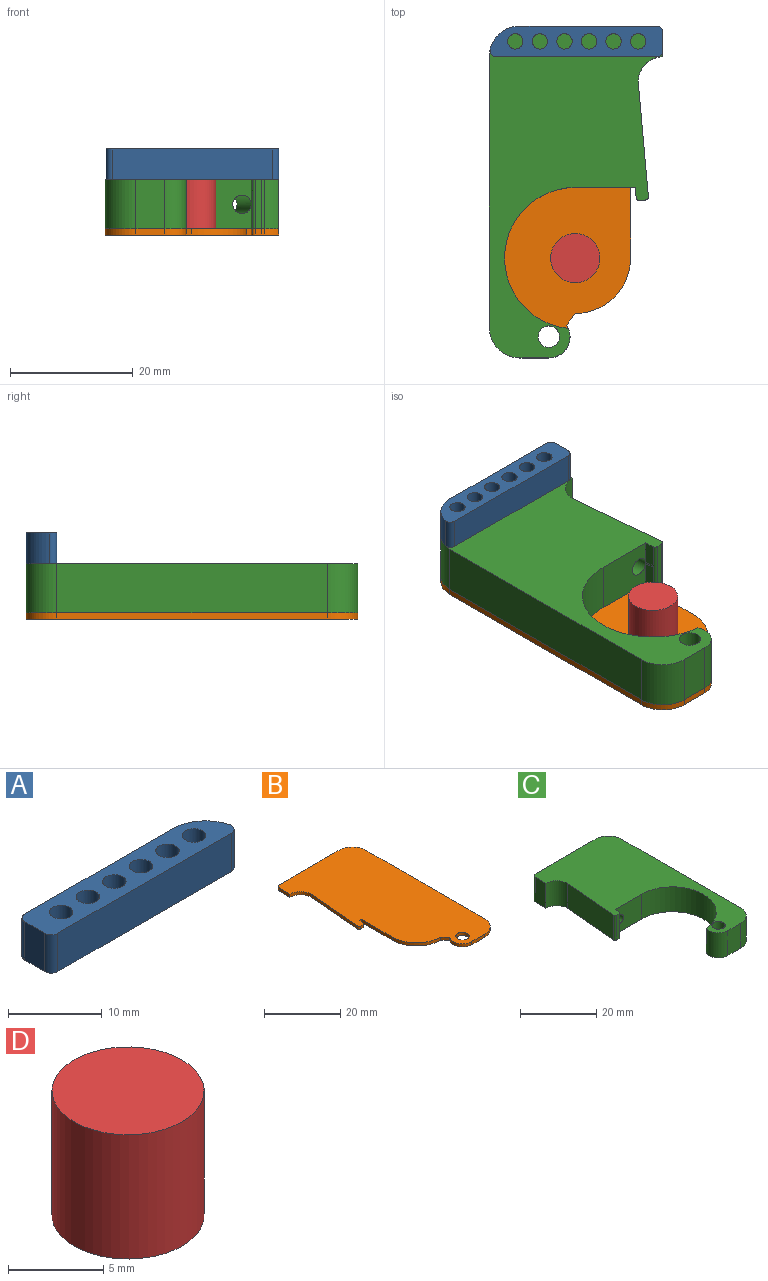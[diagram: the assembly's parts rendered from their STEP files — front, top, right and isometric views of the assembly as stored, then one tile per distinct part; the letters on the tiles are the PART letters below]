
ASSEMBLY  parts=4 mates=3
PART A: 15 faces, bbox 28.1x5x5 mm
  f0: plane 22.24x5mm, normal (0,1,0), area 111.2mm2, adj f1,f12,f13,f14
  f1: cylinder r=1mm len=5mm, axis (0,0,-1), area 7.9mm2, adj f0,f2,f13,f14
  f2: plane 5x3mm, normal (-1,0,0), area 15mm2, adj f1,f3,f13,f14
  f3: cylinder r=1mm len=5mm, axis (0,0,-1), area 7.9mm2, adj f2,f4,f13,f14
  f4: plane 26.12x5mm, normal (0,-1,0), area 130.6mm2, adj f3,f5,f13,f14
  f5: cylinder r=1mm len=5mm, axis (0,0,-1), area 9.1mm2, adj f4,f12,f13,f14
  f6: cylinder r=1.25mm len=5mm, axis (0,0,-1), area 39.3mm2, adj f13,f14
  f7: cylinder r=1.25mm len=5mm, axis (0,0,-1), area 39.3mm2, adj f13,f14
  f8: cylinder r=1.25mm len=5mm, axis (0,0,-1), area 39.3mm2, adj f13,f14
  f9: cylinder r=1.25mm len=5mm, axis (0,0,-1), area 39.3mm2, adj f13,f14
  f10: cylinder r=1.25mm len=5mm, axis (0,0,-1), area 39.3mm2, adj f13,f14
  f11: cylinder r=1.25mm len=5mm, axis (0,0,-1), area 39.3mm2, adj f13,f14
  f12: cylinder r=5mm len=5mm, axis (0,0,-1), area 33mm2, adj f0,f5,f13,f14
  f13: plane 28.12x5mm, normal (0,0,1), area 105.7mm2, adj f0,f1,f2,f3,f4,f5,f6,f7
  f14: plane 28.12x5mm, normal (0,0,-1), area 105.7mm2, adj f0,f1,f2,f3,f4,f5,f6,f7
PART B: 21 faces, bbox 28.2x54x1 mm
  f0: plane 22.24x1mm, normal (0,1,0), area 22.2mm2, adj f1,f18,f19,f20
  f1: cylinder r=1mm len=1mm, axis (0,0,-1), area 1.6mm2, adj f0,f2,f19,f20
  f2: plane 4x1mm, normal (-1,0,0), area 4mm2, adj f1,f3,f19,f20
  f3: cylinder r=4mm len=4mm, axis (0,0,-1), area 6.3mm2, adj f2,f4,f19,f20
  f4: plane 18.76x1.66mm, normal (-1,0.09,0), area 18.8mm2, adj f3,f5,f19,f20
  f5: cylinder r=0.5mm len=1mm, axis (0,0,-1), area 0.8mm2, adj f4,f6,f19,f20
  f6: plane 1x1mm, normal (-0.09,-1,0), area 1mm2, adj f5,f7,f19,f20
  f7: cylinder r=0.5mm len=1mm, axis (0,0,-1), area 0.8mm2, adj f6,f8,f19,f20
  f8: plane 1.67x1mm, normal (1,-0.09,0), area 1.7mm2, adj f7,f9,f19,f20
  f9: plane 1x0.76mm, normal (0,-1,0), area 0.8mm2, adj f8,f10,f19,f20
  f10: plane 11.5x1mm, normal (-1,0,0), area 11.5mm2, adj f9,f11,f19,f20
  f11: cylinder r=9mm len=9mm, axis (0,0,-1), area 14.1mm2, adj f10,f12,f19,f20
  f12: plane 1.91x1.41mm, normal (-0.8,-0.59,0), area 2.4mm2, adj f11,f13,f19,f20
  f13: cylinder r=3.45mm len=5.33mm, axis (0,0,-1), area 7.4mm2, adj f12,f14,f19,f20
  f14: plane 4.69x1mm, normal (0,-1,0), area 4.7mm2, adj f13,f15,f19,f20
  f15: cylinder r=5mm len=5mm, axis (0,0,-1), area 7.9mm2, adj f14,f16,f19,f20
  f16: plane 44.01x1mm, normal (1,0,0), area 44mm2, adj f15,f18,f19,f20
  f17: cylinder r=1.75mm len=3.5mm, axis (0,0,-1), area 11mm2, adj f19,f20
  f18: cylinder r=5mm len=5mm, axis (0,0,-1), area 7.9mm2, adj f0,f16,f19,f20
  f19: plane 54.01x28.24mm, normal (0,0,1), area 1203.6mm2, adj f0,f1,f2,f3,f4,f5,f6,f7
  f20: plane 54.01x28.24mm, normal (0,0,-1), area 1203.6mm2, adj f0,f1,f2,f3,f4,f5,f6,f7
PART C: 21 faces, bbox 28.2x54x8 mm
  f0: plane 3.85x1.67mm, normal (1,-0.09,0), area 6.4mm2, adj f8,f10,f18,f20
  f1: plane 22.24x8mm, normal (0,1,0), area 170.9mm2, adj f2,f16,f18,f19,f20
  f2: cylinder r=1mm len=8mm, axis (0,0,-1), area 12.6mm2, adj f1,f3,f18,f19
  f3: plane 8x4mm, normal (-1,0,0), area 32mm2, adj f2,f4,f18,f19
  f4: cylinder r=4mm len=8mm, axis (0,0,-1), area 50.3mm2, adj f3,f5,f18,f19
  f5: plane 18.76x8mm, normal (-1,0.09,0), area 150.6mm2, adj f4,f6,f18,f19
  f6: cylinder r=0.5mm len=8mm, axis (0,0,-1), area 6.3mm2, adj f5,f7,f18,f19
  f7: plane 8x1mm, normal (-0.09,-1,0), area 8mm2, adj f6,f8,f18,f19
  f8: cylinder r=0.5mm len=8mm, axis (0,0,-1), area 6.3mm2, adj f0,f7,f9,f18,f19,f20
  f9: plane 3.85x1.67mm, normal (1,-0.09,0), area 6.4mm2, adj f8,f10,f19,f20
  f10: plane 9.76x8mm, normal (0,-1,0), area 71mm2, adj f0,f9,f11,f18,f19,f20
  f11: cylinder r=11.5mm len=22.95mm, axis (0,0,-1), area 280mm2, adj f10,f12,f18,f19
  f12: cylinder r=3.45mm len=8mm, axis (0,0,-1), area 54.5mm2, adj f11,f13,f18,f19
  f13: plane 8x4.69mm, normal (0,-1,0), area 37.5mm2, adj f12,f14,f18,f19
  f14: cylinder r=5mm len=8mm, axis (0,0,-1), area 62.8mm2, adj f13,f15,f18,f19
  f15: plane 44.01x8mm, normal (1,0,0), area 352.1mm2, adj f14,f16,f18,f19
  f16: cylinder r=5mm len=8mm, axis (0,0,-1), area 62.8mm2, adj f1,f15,f18,f19
  f17: cylinder r=1.75mm len=8mm, axis (0,0,-1), area 88mm2, adj f18,f19
  f18: plane 54.01x28.24mm, normal (0,0,1), area 830.8mm2, adj f0,f1,f2,f3,f4,f5,f6,f7
  f19: plane 54.01x28.24mm, normal (0,0,-1), area 830.8mm2, adj f1,f2,f3,f4,f5,f6,f7,f8
  f20: bspline ~27.93x5.44mm, area 249mm2, adj f0,f1,f8,f9,f10
PART D: 3 faces, bbox 8x8x8 mm
  f0: cylinder r=4mm len=8mm, axis (0,0,-1), area 201.1mm2, adj f1,f2
  f1: plane 8x8mm, normal (0,0,1), area 50.3mm2, adj f0
  f2: plane 8x8mm, normal (0,0,-1), area 50.3mm2, adj f0
PLACE A rot(axis=(0,-1,0),180deg) t=(-42.81,-56.92,-9.62)mm
PLACE B rot(axis=(0,-1,0),180deg) t=(88.68,-34.85,-22.62)mm
PLACE C rot(axis=(0,-1,0),180deg) t=(41.84,-3.84,-14.62)mm
PLACE D t=(60.17,-16.8,-22.62)mm
MATE fastened A.f1 <-> C.f2  axis (0,0,-1) through (45.14,29.16,-14.62)mm
MATE fastened D.f0 <-> B.f11  axis (0,0,-1) through (31.89,-7.6,-22.62)mm
MATE fastened B.f13 <-> C.f12  axis (0,0,1) through (27.59,-20.39,-22.62)mm
